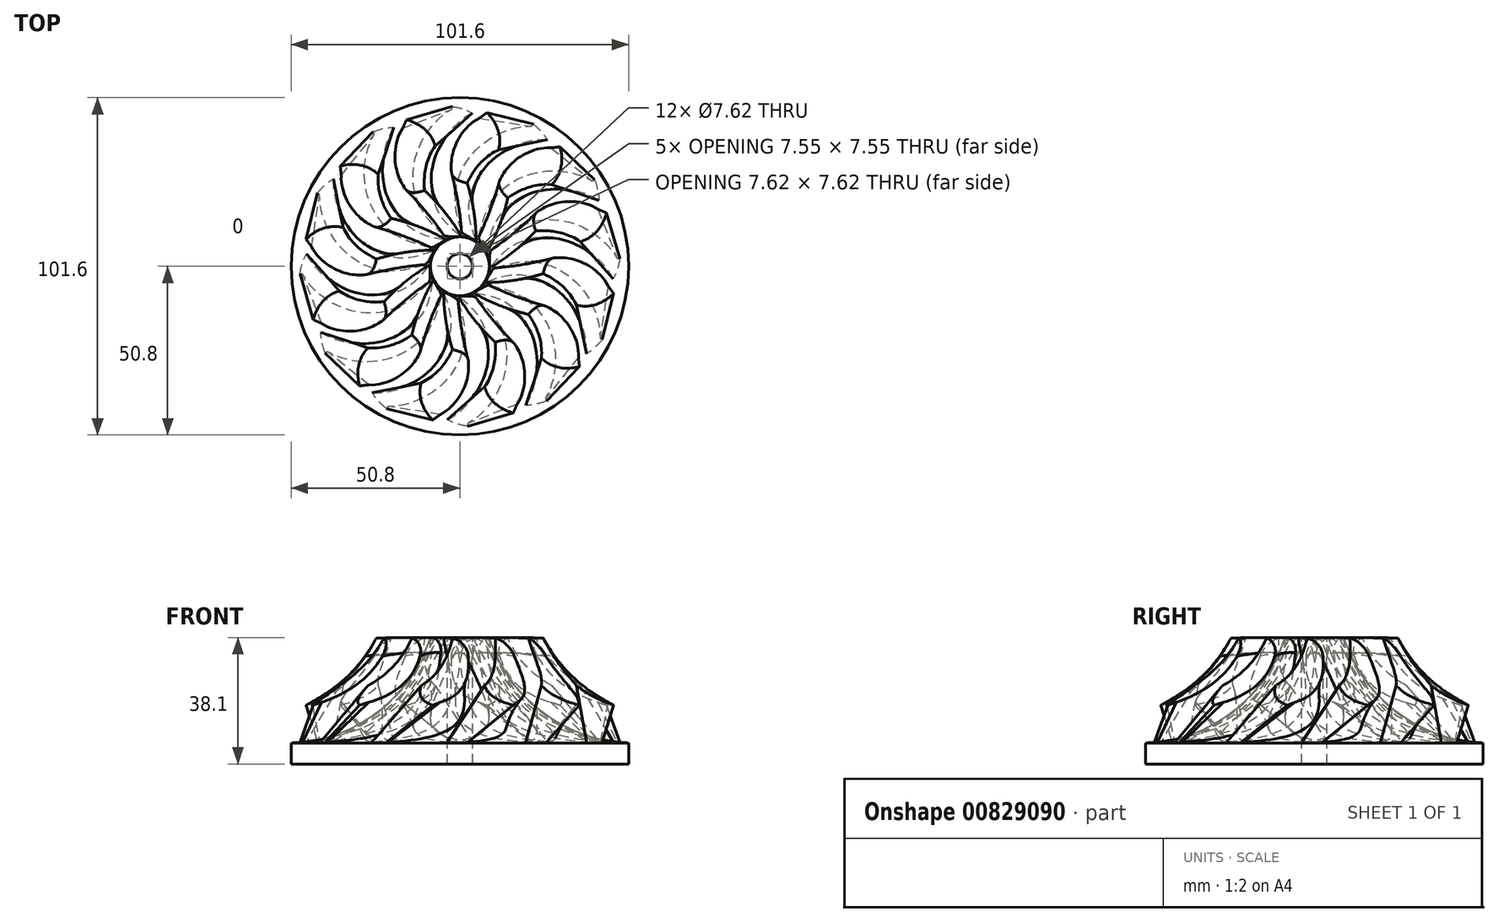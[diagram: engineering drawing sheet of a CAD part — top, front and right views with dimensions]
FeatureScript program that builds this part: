
annotation { "Feature Type Name" : "Feature", "Feature Type Description" : "" }
export const myFeature = defineFeature(function(context is Context, id is Id, definition is map)
    precondition{}
    {
        {
            var Q0;
            Q0=qCreatedBy(makeId("Front.planeOp"),FACE);
            var sketch = newSketch(context, id + "F0", { "sketchPlane" : qUnion([Q0])});
            skLineSegment(sketch, "E0", {"start": v(0, 0) * mm, "end": v(50.8, 0) * mm});
            skLineSegment(sketch, "E1", {"start": v(50.8, 0) * mm, "end": v(50.8, 6.35) * mm});
            skLineSegment(sketch, "E2", {"start": v(0, 0) * mm, "end": v(0, 38.1) * mm});
            skLineSegment(sketch, "E3", {"start": v(0, 38.1) * mm, "end": v(8.9, 38.1) * mm});
            skArc(sketch, "E4", {"start": v(8.9, 38.1) * mm, "mid": v(24.82, 15.6) * mm, "end": v(50.8, 6.35) * mm});
            skSolve(sketch);
        }
        {
            var Q0;
            Q0=makeQuery(id+"F0.imprint","IMPRINT",FACE,{"disambiguationData":[TD([[makeQuery(id+"F0.imprint","IMPRINT",EDGE,{"derivedFrom":sQuery(id+"F0.wireOp",EDGE,"E0")}),1.0]])]});
            var Q1;
            Q1=sQuery(id+"F0.wireOp",EDGE,"E2");
            revolve(context, id + "F1", {"surfaceOperationType" : NewSurfaceOperationType.NEW, "entities" : qUnion([Q0]), "axis" : qUnion([Q1]), "revolveType" : RevolveType.FULL});
        }
        {
            var Q0;
            Q0=makeQuery(id+"F1.opRevolve","SWEPT_FACE",FACE,{"disambiguationData":[OSD([sQuery(id+"F0.wireOp",EDGE,"E0")])]});
            var sketch = newSketch(context, id + "F2", { "sketchPlane" : qUnion([Q0])});
            skArc(sketch, "E5", {"start": v(0, 0) * mm, "mid": v(9.76, 27.34) * mm, "end": v(-8.22, 50.13) * mm});
            skArc(sketch, "E6", {"start": v(1.52, 0) * mm, "mid": v(11.55, 27.2) * mm, "end": v(-5.7, 50.48) * mm});
            skLineSegment(sketch, "E7", {"start": v(1.52, 0) * mm, "end": v(0, 0) * mm});
            skArc(sketch, "E8", {"start": v(-5.7, 50.48) * mm, "mid": v(-6.96, 50.3) * mm, "end": v(-8.22, 50.13) * mm});
            skSolve(sketch);
        }
        {
            var Q0;
            Q0=makeQuery(id+"F1.opRevolve","SWEPT_FACE",FACE,{"disambiguationData":[OSD([sQuery(id+"F0.wireOp",EDGE,"E3")])]});
            var sketch = newSketch(context, id + "F3", { "sketchPlane" : qUnion([Q0])});
            skArc(sketch, "E9", {"start": v(0, 0) * mm, "mid": v(15.8, -22.22) * mm, "end": v(41.16, -32.26) * mm});
            skArc(sketch, "E10", {"start": v(-4.63, 0) * mm, "mid": v(13.1, -24.85) * mm, "end": v(41.16, -36.87) * mm});
            skLineSegment(sketch, "E11", {"start": v(41.16, -36.87) * mm, "end": v(41.16, -32.26) * mm});
            skLineSegment(sketch, "E12", {"start": v(-4.63, 0) * mm, "end": v(0, 0) * mm});
            skSolve(sketch);
        }
        {
            var Q1;
            {var subQ0=sQuery(id+"F3.wireOp",EDGE,"E11");Q1=makeQuery(id+"F3.imprint","IMPRINT",FACE,{"disambiguationData":[TD([[makeQuery(id+"F3.imprint","IMPRINT",EDGE,{"derivedFrom":subQ0}),1.0]])]});}
            var Q2;
            Q2=makeQuery(id+"F2.imprint","IMPRINT",FACE,{"disambiguationData":[TD([[makeQuery(id+"F2.imprint","IMPRINT",EDGE,{"derivedFrom":sQuery(id+"F2.wireOp",EDGE,"E5")}),-1.0]])]});
            loft(context, id + "F4", {"operationType" : NewBodyOperationType.ADD, "sheetProfilesArray" : [{ "sheetProfileEntities" : qUnion([Q1]) }, { "sheetProfileEntities" : qUnion([Q2]) }]});
        }
        {
            var Q0;
            Q0=qCreatedBy(makeId("Front.planeOp"),FACE);
            var sketch = newSketch(context, id + "F5", { "sketchPlane" : qUnion([Q0])});
            skLineSegment(sketch, "E13", {"start": v(0, 0) * mm, "end": v(-50.8, 0) * mm});
            skLineSegment(sketch, "E14", {"start": v(-50.8, 0) * mm, "end": v(-50.8, 16.32) * mm});
            skLineSegment(sketch, "E15", {"start": v(0, 0) * mm, "end": v(0, -13.83) * mm});
            skLineSegment(sketch, "E16", {"start": v(0, -13.83) * mm, "end": v(-66.48, -13.83) * mm});
            skLineSegment(sketch, "E17", {"start": v(-66.48, -13.83) * mm, "end": v(-66.48, 40.67) * mm});
            skLineSegment(sketch, "E18", {"start": v(-66.48, 40.67) * mm, "end": v(-23.9, 40.67) * mm});
            skArc(sketch, "E19", {"start": v(-50.8, 16.32) * mm, "mid": v(-34.7, 25.57) * mm, "end": v(-23.9, 40.67) * mm});
            skSolve(sketch);
        }
        {
            var Q0;
            Q0=makeQuery(id+"F5.imprint","IMPRINT",FACE,{"disambiguationData":[TD([[makeQuery(id+"F5.imprint","IMPRINT",EDGE,{"derivedFrom":sQuery(id+"F5.wireOp",EDGE,"E13")}),1.0]])]});
            var Q1;
            Q1=sQuery(id+"F5.wireOp",EDGE,"E15");
            revolve(context, id + "F6", {"operationType" : NewBodyOperationType.REMOVE, "surfaceOperationType" : NewSurfaceOperationType.NEW, "entities" : qUnion([Q0]), "axis" : qUnion([Q1]), "revolveType" : RevolveType.FULL, "oppositeDirection" : true});
        }
        {
            var Q0;
            Q0=makeQuery(id+"F4.opLoft","MID_CAP_EDGE",EDGE,{"disambiguationData":[OSD([sQuery(id+"F0.wireOp",EDGE,"E3"),sQuery(id+"F0.wireOp",EDGE,"E4"),sQuery(id+"F3.wireOp",EDGE,"E9"),sQuery(id+"F3.wireOp",EDGE,"E11")])],"capPos":0.0});
            fillet(context, id + "F7", {"entities" : qUnion([Q0]), "radius" : 5.08 * mm, "tangentPropagation" : true, "allowEdgeOverflow" : false});
        }
        {
            var Q0;
            {var subQ0=sQuery(id+"F3.wireOp",EDGE,"E11");var subQ2=sQuery(id+"F0.wireOp",EDGE,"E3");Q0=makeQuery(id+"F4.boolean.opBoolean","MERGE",FACE,{"derivedFrom":[makeQuery(id+"F1.opRevolve","SWEPT_FACE",FACE,{"disambiguationData":[OSD([subQ2])]}),makeQuery(id+"F4.opLoft","CAP_FACE",FACE,{"disambiguationData":[OSD([makeQuery(id+"F3.imprint","IMPRINT",FACE,{"disambiguationData":[TD([[makeQuery(id+"F3.imprint","IMPRINT",EDGE,{"derivedFrom":subQ0}),1.0]])]})])],"isStart":true})]});}
            var sketch = newSketch(context, id + "F8", { "sketchPlane" : qUnion([Q0])});
            skCircle(sketch, "E20", {"center": v(0, 0) * mm, "radius": 3.81 * mm});
            skSolve(sketch);
        }
        {
            var Q0;
            Q0=makeQuery(id+"F8.imprint","IMPRINT",FACE,{"disambiguationData":[TD([[makeQuery(id+"F8.imprint","IMPRINT",EDGE,{"derivedFrom":sQuery(id+"F8.wireOp",EDGE,"E20")}),1.0]])]});
            extrude(context, id + "F9", {"entities" : qUnion([Q0]), "operationType" : NewBodyOperationType.REMOVE, "endBound" : BoundingType.THROUGH_ALL, "oppositeDirection" : true, "depth" : 25.4 * mm, "offsetDistance" : 25.4 * mm});
        }
        {
            var Q0;
            {var subQ0=sQuery(id+"F3.wireOp",EDGE,"E11");var subQ2=sQuery(id+"F0.wireOp",EDGE,"E3");Q0=makeQuery(id+"F4.boolean.opBoolean","MERGE",FACE,{"derivedFrom":[makeQuery(id+"F1.opRevolve","SWEPT_FACE",FACE,{"disambiguationData":[OSD([subQ2])]}),makeQuery(id+"F4.opLoft","CAP_FACE",FACE,{"disambiguationData":[OSD([makeQuery(id+"F3.imprint","IMPRINT",FACE,{"disambiguationData":[TD([[makeQuery(id+"F3.imprint","IMPRINT",EDGE,{"derivedFrom":subQ0}),1.0]])]})])],"isStart":true})]});}
            var sketch = newSketch(context, id + "F10", { "sketchPlane" : qUnion([Q0])});
            skPoint(sketch, "E21", {"position": v(0, 0) * mm});
            skPoint(sketch, "E22", {"position": v(8.9, 0) * mm});
            skSolve(sketch);
        }
        {
            var Q0;
            Q0=makeQuery(id+"F1.opRevolve","SWEPT_FACE",FACE,{"disambiguationData":[OSD([sQuery(id+"F0.wireOp",EDGE,"E0")])]});
            var sketch = newSketch(context, id + "F11", { "sketchPlane" : qUnion([Q0])});
            skPoint(sketch, "E23", {"position": v(0, 0) * mm});
            skSolve(sketch);
        }
        {
            var Q0;
            Q0=sQuery(id+"F10.wireOp",VERTEX,"E21");
            var Q1;
            Q1=sQuery(id+"F10.wireOp",VERTEX,"E22");
            var Q2;
            Q2=sQuery(id+"F11.wireOp",VERTEX,"E23");
            cPlane(context, id + "F12", {"entities" : qUnion([Q0, Q1, Q2]), "cplaneType" : CPlaneType.THREE_POINT, "offset" : 25.4 * mm, "width" : 152.4 * mm, "height" : 152.4 * mm});
        }
        {
            var Q0;
            Q0=qCreatedBy(id+"F12.planeOp",FACE);
            var sketch = newSketch(context, id + "F13", { "sketchPlane" : qUnion([Q0])});
            skLineSegment(sketch, "E24", {"start": v(0, 38.55) * mm, "end": v(0, 0) * mm, "construction": true});
            skSolve(sketch);
        }
        {
            var Q0;
            Q0=makeQuery(id+"F1.opRevolve","SWEPT_BODY",BODY,{"disambiguationData":[OSD([sQuery(id+"F0.wireOp",EDGE,"E0"),sQuery(id+"F0.wireOp",EDGE,"E1"),sQuery(id+"F0.wireOp",EDGE,"E2"),sQuery(id+"F0.wireOp",EDGE,"E3"),sQuery(id+"F0.wireOp",EDGE,"E4")])]});
            var Q1;
            Q1=sQuery(id+"F13.wireOp",EDGE,"E24");
            circularPattern(context, id + "F14", {"entities" : qUnion([Q0]), "axis" : qUnion([Q1]), "angle" : 360 * degree, "instanceCount" : 12, "equalSpace" : true, "fullFeaturePattern" : false});
        }
    });
